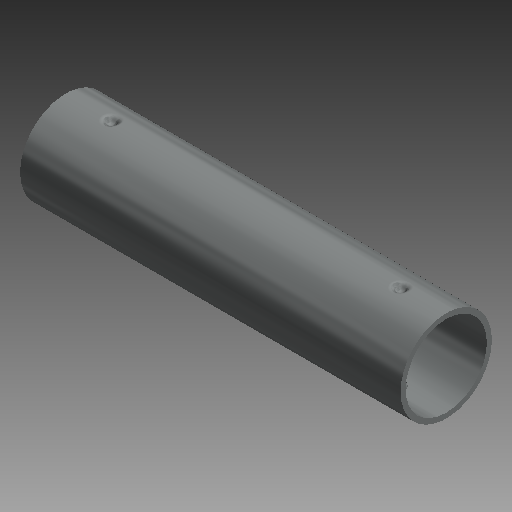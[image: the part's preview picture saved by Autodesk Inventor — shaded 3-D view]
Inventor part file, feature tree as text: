
AUTODESK INVENTOR PART (.ipt)
format: ipt  version: 2019 (Build 230136000, 136)  size: 204,800 bytes
history: native  units: mm (DEFAULTED — no unit token found)
features: mirror x1
ambient origin geometry x8: Origin, YZ Plane, XZ Plane, XY Plane, X Axis, Y Axis, Z Axis, Center Point
bodies: Solid1 (feature_tree)
feature tree (1):
  mirror  "Mirror2"
